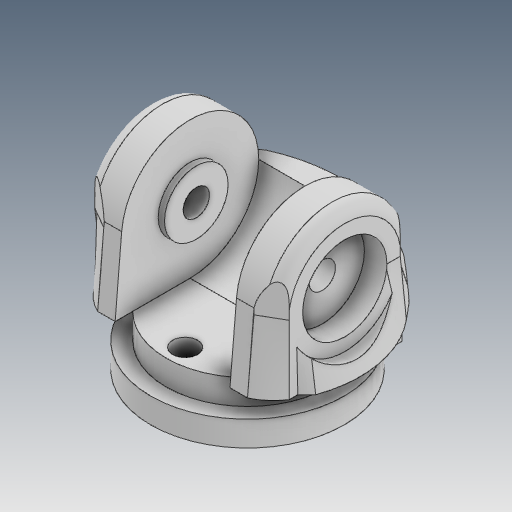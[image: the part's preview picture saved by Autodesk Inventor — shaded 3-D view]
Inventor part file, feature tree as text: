
AUTODESK INVENTOR PART (.ipt)
format: ipt  version: 2020 (Build 240168000, 168)  size: 361,472 bytes
history: native  units: mm
features: other x3, extrude x1, sketch x1
ambient origin geometry x8: Origin, YZ Plane, XZ Plane, XY Plane, X Axis, Y Axis, Z Axis, Center Point
bodies: Solid1 (feature_tree)
feature tree (5):
  other  "Base.ipt"
  extrude  "Extrusion1"  Depth=10.0mm
  other  "Solid1::Base.ipt"
  other  "TaggingFeature1"
  sketch  "Sketch1"  dims[d0=13.0mm d1=0.627mm d2=1.637mm d3=10.0mm d4=0.0mm]
